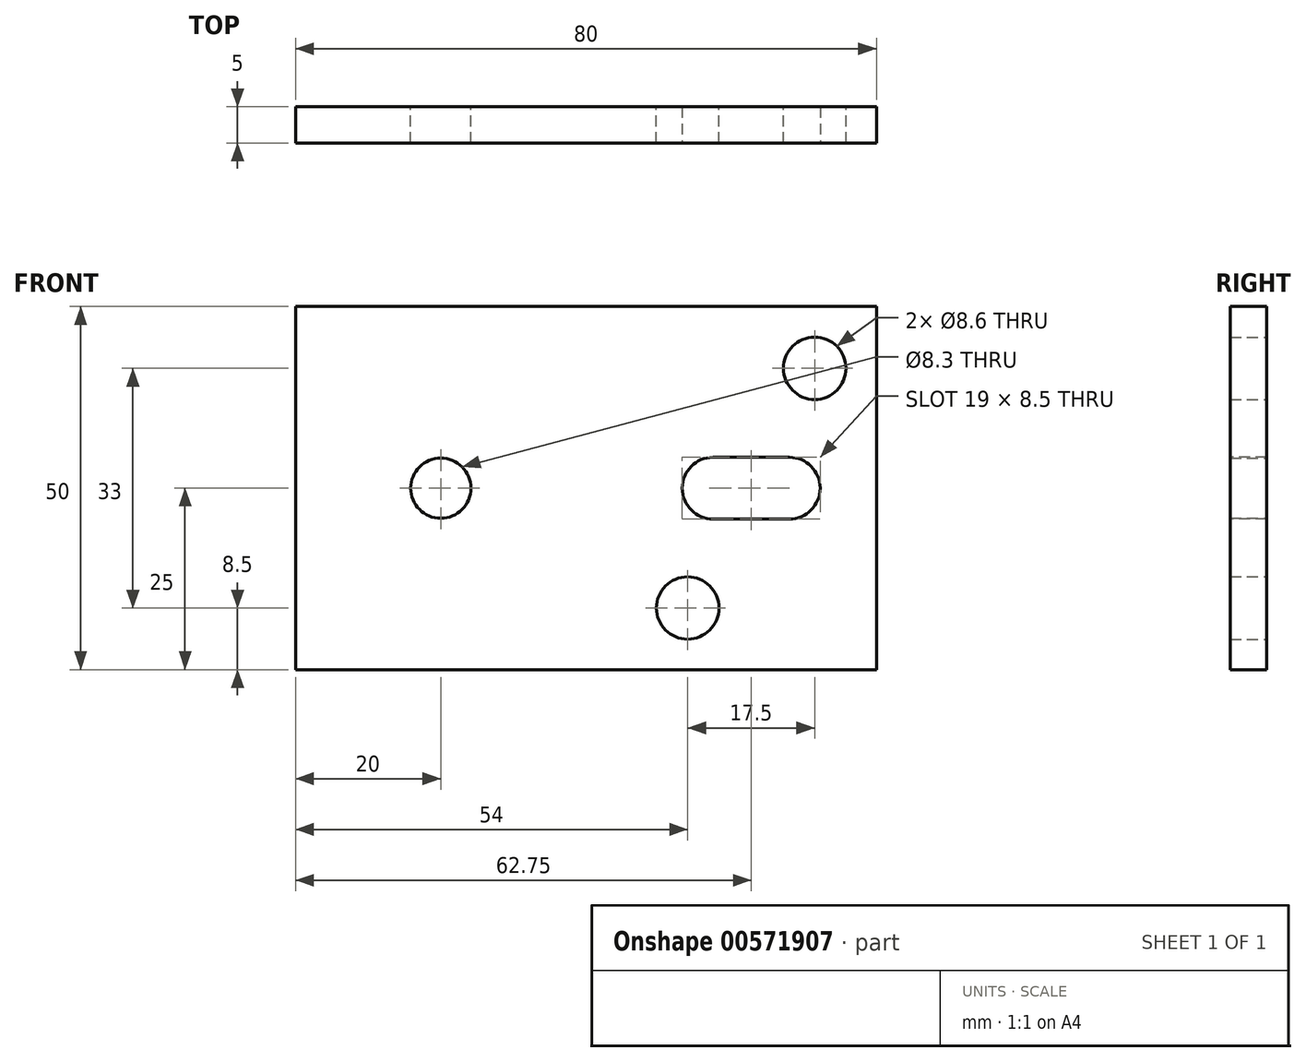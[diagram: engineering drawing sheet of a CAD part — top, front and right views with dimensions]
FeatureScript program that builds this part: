
annotation { "Feature Type Name" : "Feature", "Feature Type Description" : "" }
export const myFeature = defineFeature(function(context is Context, id is Id, definition is map)
    precondition{}
    {
        {
            var Q0;
            Q0=qCreatedBy(makeId("Front.planeOp"),FACE);
            var sketch = newSketch(context, id + "F0", { "sketchPlane" : qUnion([Q0])});
            skLineSegment(sketch, "E0.bottom", {"start": v(40, 25) * mm, "end": v(-40, 25) * mm});
            skLineSegment(sketch, "E0.top", {"start": v(40, -25) * mm, "end": v(-40, -25) * mm});
            skLineSegment(sketch, "E0.left", {"start": v(40, 25) * mm, "end": v(40, -25) * mm});
            skLineSegment(sketch, "E0.right", {"start": v(-40, 25) * mm, "end": v(-40, -25) * mm});
            skPoint(sketch, "E0.middle", {"position": v(0, 0) * mm});
            skCircle(sketch, "E1", {"center": v(31.5, 16.5) * mm, "radius": 4.3 * mm});
            skCircle(sketch, "E2", {"center": v(14, -16.5) * mm, "radius": 4.3 * mm});
            skCircle(sketch, "E3", {"center": v(-20, 0) * mm, "radius": 4.15 * mm});
            skSolve(sketch);
        }
        {
            var Q0;
            Q0 = qSketchRegion(id + "F0", true);
            extrude(context, id + "F1", {"entities" : qUnion([Q0]), "depth" : 5 * mm, "offsetDistance" : 25 * mm});
        }
        {
            var Q0;
            Q0=makeQuery(id+"F1.opExtrude","CAP_FACE",FACE,{"disambiguationData":[OSD([sQuery(id+"F0.wireOp",EDGE,"E0.bottom"),sQuery(id+"F0.wireOp",EDGE,"E0.top"),sQuery(id+"F0.wireOp",EDGE,"E0.left"),sQuery(id+"F0.wireOp",EDGE,"E0.right"),sQuery(id+"F0.wireOp",EDGE,"E1"),sQuery(id+"F0.wireOp",EDGE,"E2"),sQuery(id+"F0.wireOp",EDGE,"E3")])],"isStart":false});
            var sketch = newSketch(context, id + "F2", { "sketchPlane" : qUnion([Q0])});
            skLineSegment(sketch, "E4.bottom", {"start": v(28, -4.25) * mm, "end": v(17.5, -4.25) * mm});
            skLineSegment(sketch, "E4.top", {"start": v(28, 4.25) * mm, "end": v(17.5, 4.25) * mm});
            skArc(sketch, "E5", {"start": v(17.5, 4.25) * mm, "mid": v(13.25, 0) * mm, "end": v(17.5, -4.25) * mm});
            skArc(sketch, "E6", {"start": v(28, -4.25) * mm, "mid": v(32.25, 0) * mm, "end": v(28, 4.25) * mm});
            skSolve(sketch);
        }
        {
            var Q0;
            Q0=makeQuery(id+"F2.imprint","IMPRINT",FACE,{"disambiguationData":[TD([[makeQuery(id+"F2.imprint","IMPRINT",EDGE,{"derivedFrom":sQuery(id+"F2.wireOp",EDGE,"E4.bottom")}),-1.0]])]});
            extrude(context, id + "F3", {"entities" : qUnion([Q0]), "operationType" : NewBodyOperationType.REMOVE, "oppositeDirection" : true, "depth" : 25 * mm, "offsetDistance" : 25 * mm});
        }
    });
